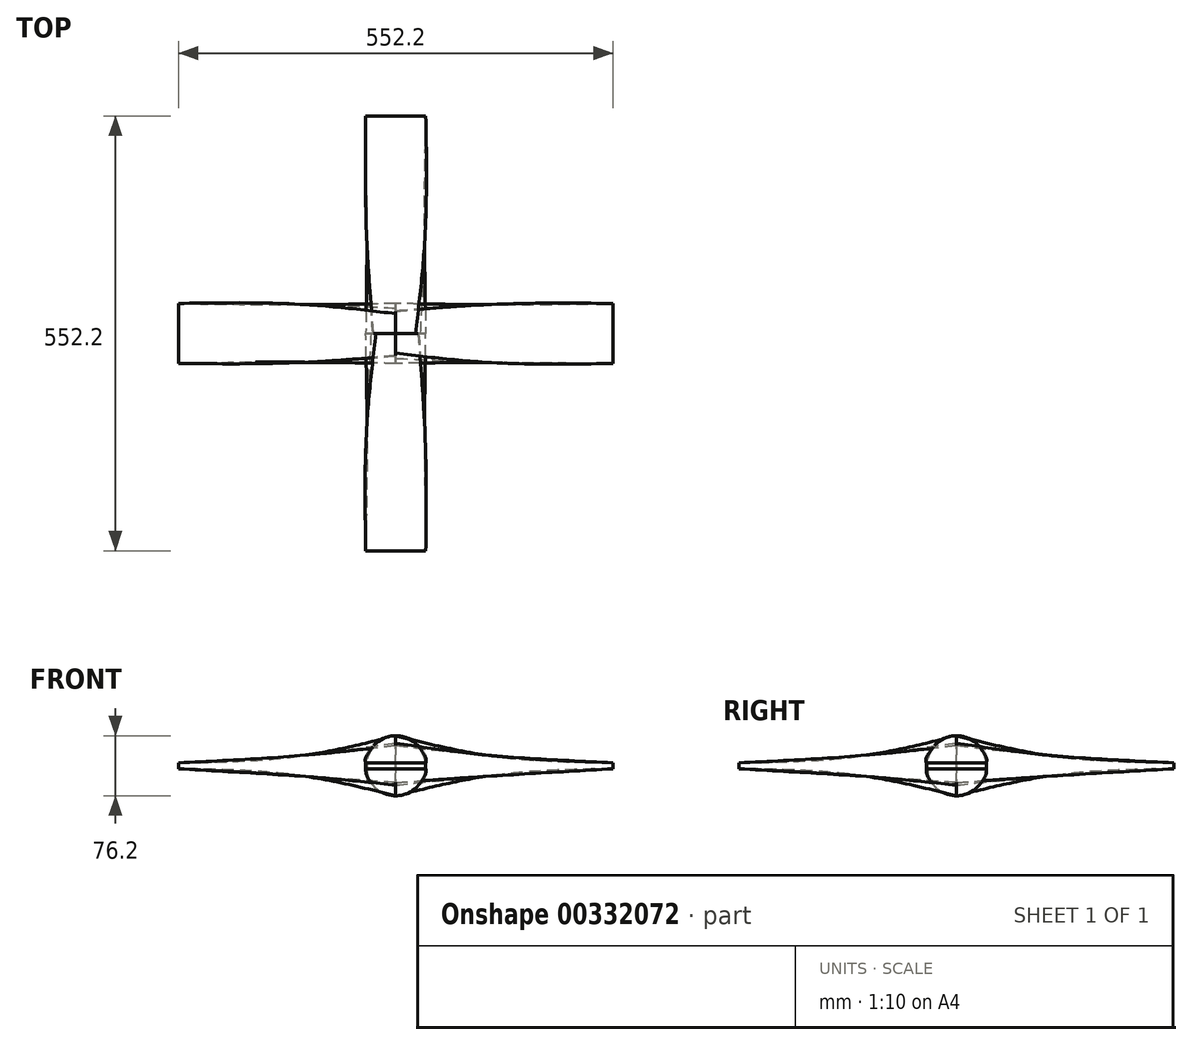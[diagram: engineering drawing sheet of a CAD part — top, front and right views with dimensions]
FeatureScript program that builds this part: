
annotation { "Feature Type Name" : "Feature", "Feature Type Description" : "" }
export const myFeature = defineFeature(function(context is Context, id is Id, definition is map)
    precondition{}
    {
        {
            var Q0;
            Q0=qCreatedBy(makeId("Front.planeOp"),FACE);
            cPlane(context, id + "F0", {"entities" : qUnion([Q0]), "cplaneType" : CPlaneType.OFFSET, "offset" : 276.1 * mm, "width" : 152.4 * mm, "height" : 152.4 * mm});
        }
        {
            var Q0;
            Q0=qCreatedBy(makeId("Front.planeOp"),FACE);
            var sketch = newSketch(context, id + "F1", { "sketchPlane" : qUnion([Q0])});
            skArc(sketch, "E0", {"start": v(-25.1, 28.66) * mm, "mid": v(-37.8, 4.85) * mm, "end": v(-31.52, -21.4) * mm});
            skArc(sketch, "E1", {"start": v(28.17, 25.65) * mm, "mid": v(2.15, 38.04) * mm, "end": v(-25.1, 28.66) * mm});
            skArc(sketch, "E2", {"start": v(-31.52, -21.4) * mm, "mid": v(-1.94, -38.05) * mm, "end": v(29.19, -24.5) * mm});
            skArc(sketch, "E3", {"start": v(29.19, -24.5) * mm, "mid": v(38.1, 0.77) * mm, "end": v(28.17, 25.65) * mm});
            skSolve(sketch);
        }
        {
            var Q0;
            Q0=qCreatedBy(id+"F0.planeOp",FACE);
            var sketch = newSketch(context, id + "F2", { "sketchPlane" : qUnion([Q0])});
            skLineSegment(sketch, "E4.bottom", {"start": v(38.1, -3.8) * mm, "end": v(-38.1, -3.81) * mm});
            skLineSegment(sketch, "E4.top", {"start": v(38.1, 3.81) * mm, "end": v(-38.1, 3.8) * mm});
            skLineSegment(sketch, "E4.left", {"start": v(38.1, -3.8) * mm, "end": v(38.1, 3.81) * mm});
            skLineSegment(sketch, "E4.right", {"start": v(-38.1, -3.81) * mm, "end": v(-38.1, 3.8) * mm});
            skPoint(sketch, "E4.middle", {"position": v(0, 0) * mm});
            skSolve(sketch);
        }
        {
            var Q0;
            Q0=qCreatedBy(makeId("Front.planeOp"),FACE);
            cPlane(context, id + "F3", {"entities" : qUnion([Q0]), "cplaneType" : CPlaneType.OFFSET, "offset" : 114.3 * mm, "width" : 152.4 * mm, "height" : 152.4 * mm});
        }
        {
            var Q0;
            Q0=qCreatedBy(id+"F3.planeOp",FACE);
            var sketch = newSketch(context, id + "F4", { "sketchPlane" : qUnion([Q0])});
            skLineSegment(sketch, "E5.bottom", {"start": v(36.6, 13.52) * mm, "end": v(-36.6, 13.52) * mm});
            skLineSegment(sketch, "E5.top", {"start": v(36.6, -13.52) * mm, "end": v(-36.6, -13.52) * mm});
            skLineSegment(sketch, "E5.left", {"start": v(36.6, 13.52) * mm, "end": v(36.6, -13.52) * mm});
            skLineSegment(sketch, "E5.right", {"start": v(-36.6, 13.52) * mm, "end": v(-36.6, -13.52) * mm});
            skPoint(sketch, "E5.middle", {"position": v(0, 0) * mm});
            skSolve(sketch);
        }
        {
            var Q0;
            Q0=makeQuery(id+"F1.imprint","IMPRINT",FACE,{"disambiguationData":[TD([[makeQuery(id+"F1.imprint","IMPRINT",EDGE,{"derivedFrom":sQuery(id+"F1.wireOp",EDGE,"E0")}),1.0]])]});
            var Q1;
            Q1=makeQuery(id+"F4.imprint","IMPRINT",FACE,{"disambiguationData":[TD([[makeQuery(id+"F4.imprint","IMPRINT",EDGE,{"derivedFrom":sQuery(id+"F4.wireOp",EDGE,"E5.bottom")}),1.0]])]});
            var Q2;
            Q2=makeQuery(id+"F2.imprint","IMPRINT",FACE,{"disambiguationData":[TD([[makeQuery(id+"F2.imprint","IMPRINT",EDGE,{"derivedFrom":sQuery(id+"F2.wireOp",EDGE,"E4.bottom")}),-1.0]])]});
            loft(context, id + "F5", {"sheetProfilesArray" : [{ "sheetProfileEntities" : qUnion([Q0]) }, { "sheetProfileEntities" : qUnion([Q1]) }, { "sheetProfileEntities" : qUnion([Q2]) }]});
        }
        {
            var Q0;
            Q0=qCreatedBy(makeId("Front.planeOp"),FACE);
            var sketch = newSketch(context, id + "F6", { "sketchPlane" : qUnion([Q0])});
            skLineSegment(sketch, "E6", {"start": v(0, 76.23) * mm, "end": v(0, -78.41) * mm, "construction": true});
            skSolve(sketch);
        }
        {
            var Q0;
            Q0=makeQuery(id+"F5.opLoft","SWEPT_BODY",BODY,{"disambiguationData":[OSD([makeQuery(id+"F1.imprint","IMPRINT",FACE,{"disambiguationData":[TD([[makeQuery(id+"F1.imprint","IMPRINT",EDGE,{"derivedFrom":sQuery(id+"F1.wireOp",EDGE,"E0")}),1.0]])]}),makeQuery(id+"F2.imprint","IMPRINT",FACE,{"disambiguationData":[TD([[makeQuery(id+"F2.imprint","IMPRINT",EDGE,{"derivedFrom":sQuery(id+"F2.wireOp",EDGE,"E4.bottom")}),-1.0]])]}),sQuery(id+"F4.wireOp",EDGE,"E5.bottom")])]});
            var Q1;
            Q1=sQuery(id+"F6.wireOp",EDGE,"E6");
            circularPattern(context, id + "F7", {"entities" : qUnion([Q0]), "axis" : qUnion([Q1]), "angle" : 360 * degree, "instanceCount" : 4, "oppositeDirection" : true, "equalSpace" : true});
        }
    });
